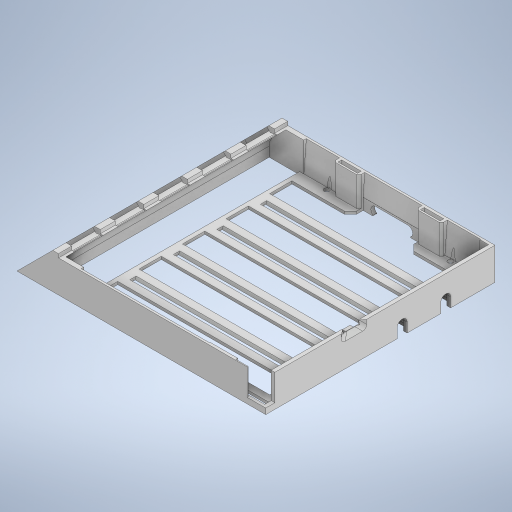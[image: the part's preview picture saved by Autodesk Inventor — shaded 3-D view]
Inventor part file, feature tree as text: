
AUTODESK INVENTOR PART (.ipt)
format: ipt  version: 2023 (Build 270158000, 158)  size: 1,472,512 bytes
history: native  units: mm
features: projected_geometry x64, sketch x40, extrude x38, chamfer x6, plane x3, mirror x3, hole x2, fillet x2, pattern_linear x1
ambient origin geometry x8: Origin, YZ Plane, XZ Plane, XY Plane, X Axis, Y Axis, Z Axis, Center Point
bodies: Solid1 (feature_tree)
feature tree (159):
  extrude  "Extrusion1"  Depth=9.3mm
  pattern_linear  "Rectangular Pattern1"  Count1=6 Spacing1=19.0mm
  extrude  "Extrusion2"  Depth=100.0mm
  extrude  "Extrusion3"  Depth=5.4mm TaperAngle=0.0deg
  extrude  "Extrusion4"  Depth=5.4mm TaperAngle=0.0deg
  extrude  "Extrusion5"  Depth=3.0mm TaperAngle=0.0deg
  extrude  "Extrusion6"  TaperAngle=45.0deg  [1 undecoded]
  extrude  "Extrusion7"  Depth=3.0mm
  chamfer  "Chamfer1"  [1 undecoded]
  sketch  "Sketch11"  dims[d20=0.0mm d21=0.0mm d22=3.0mm d23=0.0mm]
  extrude  "Extrusion8"  Depth=6.0mm
  plane  "Work Plane1"
  mirror  "Mirror1"
  extrude  "Extrusion12"  Depth=1.2mm
  extrude  "Extrusion11"  Depth=3.0mm TaperAngle=0.0deg
  hole  "Hole1"  [1 undecoded]
  extrude  "Extrusion14"  Depth=4.2mm
  extrude  "Extrusion16"  Depth=10.0mm TaperAngle=0.0deg
  plane  "Work Plane5"
  extrude  "Extrusion18"  Depth=11.0mm
  fillet  "Fillet5"  Radius=36.0mm
  extrude  "Extrusion23"  [1 undecoded]
  plane  "Work Plane6"
  extrude  "Extrusion24"  Depth=36.0mm
  chamfer  "Chamfer8"  Distance=1.2mm
  chamfer  "Chamfer10"  Distance=1.0mm Angle=45.0deg
  extrude  "Extrusion25"  Depth=4.0mm TaperAngle=0.0deg
  extrude  "Extrusion26"  Depth=3.4mm
  mirror  "Mirror3"
  hole  "Hole2"  [1 undecoded]
  extrude  "Extrusion27"  Depth=8.0mm
  extrude  "Extrusion28"  Depth=54.0mm
  extrude  "Extrusion29"  Depth=4.3mm
  chamfer  "Chamfer11"  Distance=10.0mm
  chamfer  "Chamfer12"  Distance=7.4mm
  fillet  "Fillet6"  Radius=35.0mm
  extrude  "Extrusion30"  Depth=1.6mm
  chamfer  "Chamfer13"  [1 undecoded]
  extrude  "Extrusion31"  Depth=2.0mm TaperAngle=45.0deg
  extrude  "Extrusion32"  Depth=22.0mm
  extrude  "Extrusion33"  Depth=2.0mm
  extrude  "Extrusion34"  Depth=3.0mm TaperAngle=0.0deg
  extrude  "Extrusion35"  Depth=0.8mm TaperAngle=0.0deg
  extrude  "Extrusion36"  Depth=0.4mm TaperAngle=0.0deg
  extrude  "Extrusion43"  Depth=2.0mm
  mirror  "Mirror4"
  extrude  "Extrusion44"  Depth=2.2mm
  extrude  "Extrusion46"  Depth=0.8mm TaperAngle=0.0deg
  extrude  "Extrusion47"  Depth=12.0mm
  extrude  "Extrusion48"  Depth=0.8mm TaperAngle=0.0deg
  extrude  "Extrusion49"  Depth=90.4mm
  extrude  "Extrusion50"  Depth=1.6mm
  extrude  "Extrusion51"  Depth=12.0mm
  extrude  "Extrusion52"  TaperAngle=0.0deg  [1 undecoded]
  extrude  "Extrusion53"  Depth=18.2mm
  extrude  "Extrusion54"  Depth=1.4mm
  sketch  "Sketch1"  dims[d0=3.4mm d1=9.3mm]
  sketch  "Sketch3"  dims[d2=2.0mm]
  sketch  "Sketch4"  dims[d3=14.0mm]
  sketch  "Sketch5"  dims[d4=76.0mm d5=0.0mm d6=60.0mm d8=19.0mm]
  sketch  "Sketch7"  dims[d10=76.0mm d11=0.0mm d12=100.0mm]
  projected_geometry  "Projected Loop1"
  sketch  "Sketch8"  dims[d13=0.0mm d14=0.0mm d15=5.4mm d16=0.0mm]
  projected_geometry  "Projected Loop2"
  projected_geometry  "Projected Loop3"
  projected_geometry  "Projected Loop4"
  projected_geometry  "Projected Loop5"
  sketch  "Sketch9"  dims[d17=1.6mm d18=5.4mm d19=0.0mm]
  projected_geometry  "Projected Loop6"
  projected_geometry  "Projected Loop7"
  projected_geometry  "Projected Loop8"
  sketch  "Sketch14"  dims[d24=2.0mm d25=2.0mm d26=45.0deg d29=45.0deg]
  sketch  "Sketch15"  dims[d30=2.0mm d31=0.0mm d37=3.0mm]
  sketch  "Sketch17"  dims[d38=23.8mm d39=0.0mm d40=0.0mm]
  sketch  "Sketch19"  dims[d43=4.0mm d44=0.0mm]
  sketch  "Sketch22"  dims[d45=0.01mm d46=6.0mm d47=4.0mm d48=2.0mm d49=90.0deg d50=8.0mm d51=0.0mm d52=6.0mm]
  sketch  "Sketch25"  dims[d53=4.0mm d58=1.2mm]
  projected_geometry  "Projected Loop11"
  projected_geometry  "Projected Loop22"
  projected_geometry  "Projected Loop23"
  sketch  "Sketch35"  dims[d59=2.0mm d61=3.0mm d62=0.0mm]
  sketch  "Sketch37"  dims[d69=8.0mm d70=0.0mm d72=2.0mm]
  projected_geometry  "Projected Loop24"
  projected_geometry  "Projected Loop25"
  sketch  "Sketch38"  dims[d73=25.0mm d79=4.2mm]
  sketch  "Sketch40"  dims[d80=14.0mm d81=10.0mm d82=0.0mm]
  projected_geometry  "Projected Loop27"
  projected_geometry  "Projected Loop30"
  projected_geometry  "Projected Loop31"
  projected_geometry  "Projected Loop32"
  projected_geometry  "Projected Loop33"
  sketch  "Sketch43"  dims[d117=0.2mm d118=11.0mm d119=36.0mm]
  sketch  "Sketch44"  dims[d120=10.0mm d121=0.0mm d125=-1.6mm]
  sketch  "Sketch45"  dims[d126=8.5mm d127=36.0mm d128=1.2mm d129=0.0mm d130=1.0mm d131=2.0mm d132=45.0deg]
  projected_geometry  "Projected Loop34"
  projected_geometry  "Projected Loop35"
  sketch  "Sketch46"  dims[d136=2.6mm d137=2.0mm d138=45.0deg d139=4.0mm d140=0.0mm]
  sketch  "Sketch47"  dims[d141=4.0mm d142=0.0mm d143=3.4mm]
  sketch  "Sketch49"  dims[d144=1.8mm d145=40.0mm d147=19.0mm d148=10.0mm d150=10.0mm]
  projected_geometry  "Projected Loop40"
  projected_geometry  "Projected Loop41"
  projected_geometry  "Projected Loop42"
  projected_geometry  "Projected Loop43"
  projected_geometry  "Projected Loop44"
  projected_geometry  "Projected Loop45"
  projected_geometry  "Projected Loop46"
  projected_geometry  "Projected Loop47"
  projected_geometry  "Projected Loop48"
  sketch  "Sketch50"  dims[d152=3.5mm d153=8.0mm]
  sketch  "Sketch51"  dims[d154=11.5mm]
  projected_geometry  "Projected Loop49"
  projected_geometry  "Projected Loop50"
  sketch  "Sketch52"  dims[d155=2.2mm d156=6.0mm d157=4.0mm d158=2.0mm d159=90.0deg d160=8.0mm d161=0.0mm d162=54.0mm]
  sketch  "Sketch53"  dims[d163=94.0mm d165=4.3mm]
  sketch  "Sketch54"  dims[d166=21.5mm]
  projected_geometry  "Projected Loop51"
  sketch  "Sketch65"  dims[d167=4.2mm]
  projected_geometry  "Projected Loop59"
  sketch  "Sketch66"  dims[d168=20.0mm d170=19.0mm d171=10.0mm d173=10.0mm d175=10.0mm d176=0.0mm]
  sketch  "Sketch70"  dims[d178=8.0mm d179=7.4mm d180=0.0mm d181=35.0mm]
  projected_geometry  "Projected Loop63"
  projected_geometry  "Projected Loop64"
  sketch  "Sketch71"  dims[d182=42.0mm d183=1.6mm d184=0.0mm d185=0.0mm]
  projected_geometry  "Projected Loop65"
  projected_geometry  "Projected Loop66"
  sketch  "Sketch72"  dims[d186=2.0mm d187=1.4mm d188=45.0deg d189=2.0mm d190=1.4mm d191=45.0deg]
  projected_geometry  "Projected Loop67"
  projected_geometry  "Projected Loop68"
  projected_geometry  "Projected Loop69"
  projected_geometry  "Projected Loop70"
  projected_geometry  "Projected Loop71"
  projected_geometry  "Projected Loop72"
  projected_geometry  "Projected Loop73"
  projected_geometry  "Projected Loop74"
  sketch  "Sketch73"  dims[d192=3.0mm d193=22.0mm]
  projected_geometry  "Projected Loop75"
  projected_geometry  "Projected Loop76"
  projected_geometry  "Projected Loop77"
  projected_geometry  "Projected Loop78"
  projected_geometry  "Projected Loop79"
  sketch  "Sketch75"  dims[d194=30.0mm d195=2.0mm]
  projected_geometry  "Projected Loop81"
  sketch  "Sketch76"  dims[d196=4.0mm d197=3.0mm d198=0.0mm]
  sketch  "Sketch77"  dims[d199=1.0mm d200=1.4mm d201=45.0deg d202=0.8mm d203=0.0mm]
  projected_geometry  "Projected Loop82"
  projected_geometry  "Projected Loop83"
  projected_geometry  "Projected Loop84"
  projected_geometry  "Projected Loop85"
  projected_geometry  "Projected Loop86"
  projected_geometry  "Projected Loop87"
  projected_geometry  "Projected Loop88"
  projected_geometry  "Projected Loop89"
  projected_geometry  "Projected Loop90"
  projected_geometry  "Projected Loop91"
  projected_geometry  "Projected Loop92"
  sketch  "Sketch78"  dims[d204=5.0mm d205=0.4mm d206=0.0mm]
  projected_geometry  "Projected Loop93"
  projected_geometry  "Projected Loop94"
  sketch  "Sketch79"  dims[d210=0.4mm d211=0.0mm d212=2.0mm d213=2.2mm d214=0.8mm d215=0.0mm d216=12.0mm d217=0.8mm d218=0.0mm d220=90.4mm d221=1.6mm d224=12.0mm d225=0.0mm d226=0.0mm d227=18.2mm d228=1.4mm d237=2.5mm d239=0.4mm d240=0.4mm d241=0.4mm d242=6.0mm d243=0.4mm d286=0.1mm d287=0.0mm d288=19.0mm d289=12.4mm d290=12.4mm d291=12.4mm d293=12.0mm d294=0.5mm d295=0.0mm d298=10.0mm d299=0.0mm d300=0.0mm d301=0.0mm d302=0.3mm d303=0.0mm d304=0.3mm d305=0.0mm d306=0.3mm d307=0.0mm d308=2.8mm d309=0.0mm d310=0.0mm d311=0.0mm d312=0.0mm d313=0.0mm d314=0.0mm d315=0.0mm d316=0.0mm d71=0.5mm]
note: 7 required parameter values undecoded (feature->parameter linkage not recoverable at this tier; creation-order binding heuristic only, values carry confidence <= 0.55)
